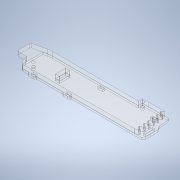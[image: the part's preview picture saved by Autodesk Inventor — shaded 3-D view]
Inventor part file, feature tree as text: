
AUTODESK INVENTOR PART (.ipt)
format: ipt  version: 2021 (Build 250183000, 183)  size: 547,328 bytes
history: native  units: mm
features: extrude x4, fillet x4, sketch x4, hole x2, other x2, plane x1, split x1
ambient origin geometry x8: Origin, YZ Plane, XZ Plane, XY Plane, X Axis, Y Axis, Z Axis, Center Point
bodies: Solid1 (feature_tree)
feature tree (18):
  extrude  "Extrusion1"  Depth=4.0mm
  extrude  "Extrusion2"  Depth=18.5mm
  plane  "Work Plane1"
  split  "Split1"
  fillet  "Fillet1"  Radius=18.5mm
  sketch  "Sketch5"  dims[d12=10.0mm d36=110.0mm d37=18.5mm]
  hole  "Hole2"  [1 undecoded]
  hole  "Hole3"  [1 undecoded]
  fillet  "Fillet2"  Radius=2.0mm
  sketch  "Sketch7"  dims[d40=2.0mm d41=9.0mm d42=2.0mm d43=1.6mm d44=2.0mm d45=4.5mm d47=65.0mm d48=9.0mm d50=10.0mm d51=3.6mm d52=7.6mm d53=5.0mm d54=1.6mm d58=4.5mm d59=2.0mm d60=90.5mm d61=4.0mm d64=3.2mm d65=1.0mm d66=4.0mm d67=0.0mm d77=11.8mm d79=29.192835mm d81=2.223092mm d82=100.0mm d83=29.192835mm d85=6.0mm d86=3.2mm d87=0.0375mm d88=0.075mm d89=0.075mm d90=0.075mm d92=57.0mm d93=47.0mm d94=6.75mm d95=1.0mm d96=2.0mm d97=0.439391mm d99=0.0mm d100=0.25mm d101=0.3mm d102=6.0mm d103=4.0mm d104=2.0mm d105=90.0deg d106=8.0mm d107=0.0mm d108=0.3mm d109=6.0mm d110=4.0mm d111=2.0mm d112=90.0deg d113=8.0mm d114=0.0mm d115=0.25mm d121=2.0mm d122=0.0mm d134=180.0deg d137=180.0deg d139=8.0mm d142=17.0mm d144=17.0mm d145=1.6mm d146=1.6mm d147=4.0mm d148=2.0mm d149=4.0mm d150=2.0mm d151=2.0mm d152=2.0mm d153=2.0mm d154=2.0mm d155=2.0mm d156=0.0mm d157=2.0mm d158=0.15mm d159=0.4mm]
  extrude  "Extrusion3"  Depth=1.6mm
  extrude  "Extrusion5"  Depth=2.0mm
  fillet  "Fillet4"  Radius=4.5mm
  fillet  "Fillet5"  Radius=65.0mm
  sketch  "Sketch3"  dims[d5=2.0mm d6=0.0mm d11=4.0mm]
  sketch  "Sketch6"  dims[d38=25.0mm d39=22.6mm]
  other  "Gear-4mm"
  other  "Plate-2mm"
note: 2 required parameter values undecoded (feature->parameter linkage not recoverable at this tier; creation-order binding heuristic only, values carry confidence <= 0.55)
